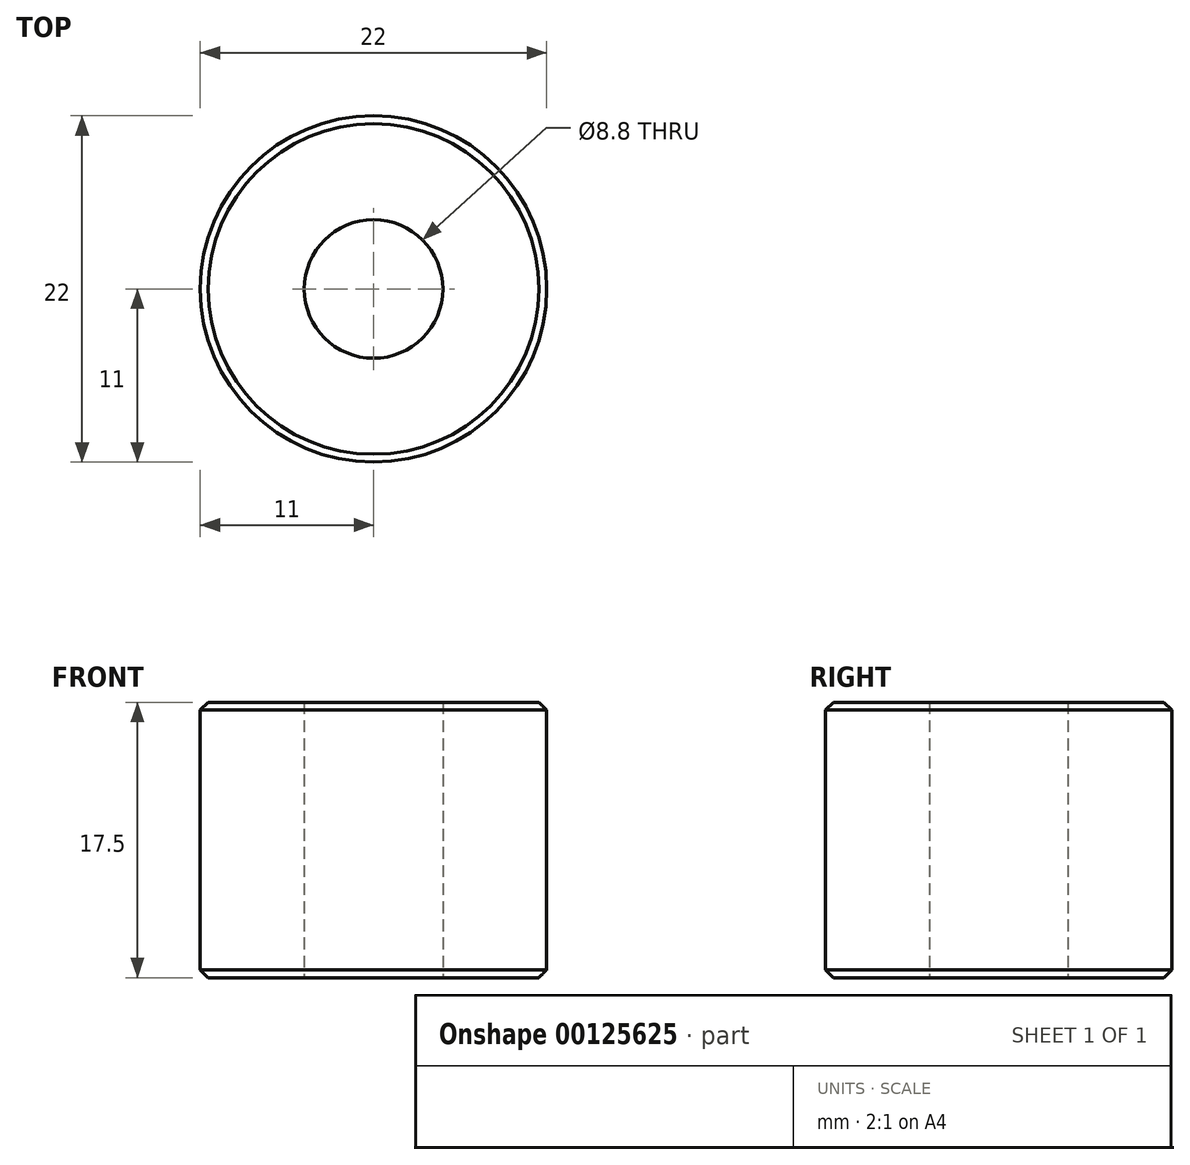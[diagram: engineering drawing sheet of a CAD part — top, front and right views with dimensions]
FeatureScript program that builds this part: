
annotation { "Feature Type Name" : "Feature", "Feature Type Description" : "" }
export const myFeature = defineFeature(function(context is Context, id is Id, definition is map)
    precondition{}
    {
        {
            var Q0;
            Q0=qCreatedBy(makeId("Top.planeOp"),FACE);
            var sketch = newSketch(context, id + "F0", { "sketchPlane" : qUnion([Q0])});
            skCircle(sketch, "E0", {"center": v(0, 0) * mm, "radius": 11 * mm});
            skCircle(sketch, "E1", {"center": v(0, 0) * mm, "radius": 4.4 * mm});
            skSolve(sketch);
        }
        {
            var Q0;
            Q0=makeQuery(id+"F0.imprint","IMPRINT",FACE,{"disambiguationData":[TD([[makeQuery(id+"F0.imprint","IMPRINT",EDGE,{"derivedFrom":sQuery(id+"F0.wireOp",EDGE,"E0")}),1.0]])]});
            extrude(context, id + "F1", {"entities" : qUnion([Q0]), "depth" : 17.5 * mm});
        }
        {
            var Q0;
            Q0=makeQuery(id+"F1.opExtrude","CAP_EDGE",EDGE,{"disambiguationData":[OSD([sQuery(id+"F0.wireOp",EDGE,"E0")])],"isStart":false});
            var Q1;
            Q1=makeQuery(id+"F1.opExtrude","CAP_EDGE",EDGE,{"disambiguationData":[OSD([sQuery(id+"F0.wireOp",EDGE,"E0")])],"isStart":true});
            chamfer(context, id + "F2", {"entities" : qUnion([Q0, Q1]), "width" : .5 * mm, "tangentPropagation" : true});
        }
    });
